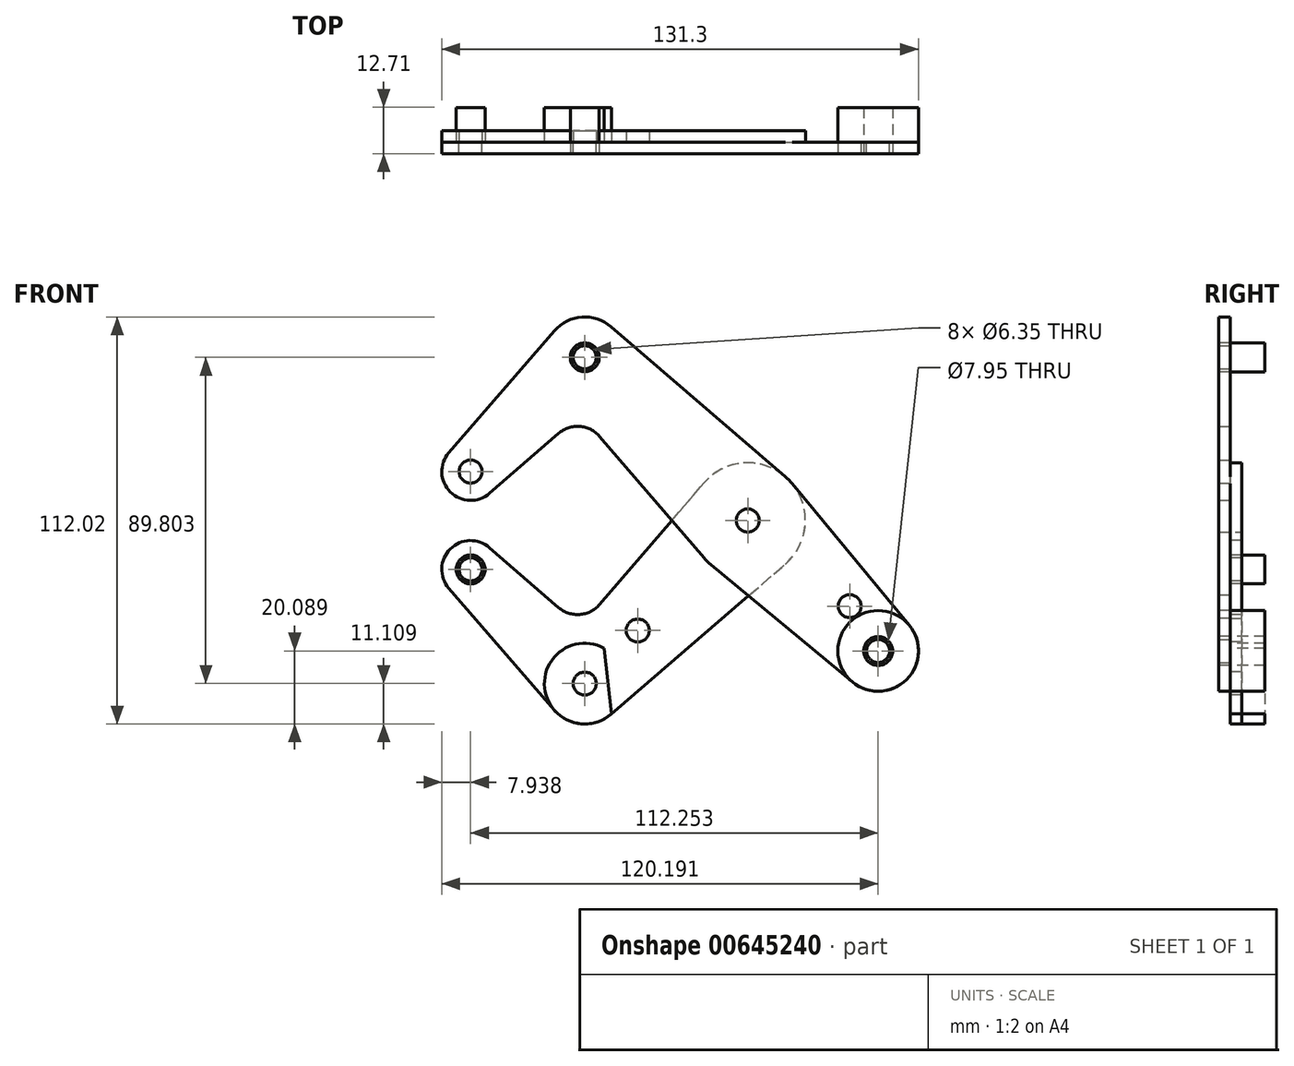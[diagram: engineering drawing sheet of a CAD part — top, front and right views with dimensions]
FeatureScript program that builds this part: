
annotation { "Feature Type Name" : "Feature", "Feature Type Description" : "" }
export const myFeature = defineFeature(function(context is Context, id is Id, definition is map)
    precondition{}
    {
        {
            var Q0;
            Q0=qCreatedBy(makeId("Front.planeOp"),FACE);
            var sketch = newSketch(context, id + "F0", { "sketchPlane" : qUnion([Q0])});
            skLineSegment(sketch, "E0", {"start": v(-76.33, 13.47) * mm, "end": v(-44.9, 44.9) * mm, "construction": true});
            skLineSegment(sketch, "E1", {"start": v(-44.9, 44.9) * mm, "end": v(35.92, -35.92) * mm, "construction": true});
            skCircle(sketch, "E2", {"center": v(-76.33, 13.47) * mm, "radius": 3.18 * mm});
            skCircle(sketch, "E3", {"center": v(-44.9, 44.9) * mm, "radius": 3.18 * mm});
            skCircle(sketch, "E4", {"center": v(35.92, -35.92) * mm, "radius": 3.18 * mm});
            skCircle(sketch, "E5", {"center": v(0, 0) * mm, "radius": 3.18 * mm});
            skCircle(sketch, "E6", {"center": v(35.92, -35.92) * mm, "radius": 11.11 * mm});
            skCircle(sketch, "E7", {"center": v(-44.9, 44.9) * mm, "radius": 11.11 * mm});
            skCircle(sketch, "E8", {"center": v(0, 0) * mm, "radius": 3.98 * mm});
            skCircle(sketch, "E9", {"center": v(-76.33, 13.47) * mm, "radius": 7.94 * mm});
            skCircle(sketch, "E10", {"center": v(0, 0) * mm, "radius": 15.88 * mm});
            skCircle(sketch, "E11", {"center": v(28.07, -23.58) * mm, "radius": 3.18 * mm});
            skLineSegment(sketch, "E12", {"start": v(0, 0) * mm, "end": v(31.58, 31.58) * mm, "construction": true});
            skLineSegment(sketch, "E13", {"start": v(0, 0) * mm, "end": v(-44.9, -44.9) * mm, "construction": true});
            skLineSegment(sketch, "E14", {"start": v(-76.33, -13.47) * mm, "end": v(-44.9, -44.9) * mm, "construction": true});
            skCircle(sketch, "E15", {"center": v(-44.9, -44.9) * mm, "radius": 3.18 * mm});
            skCircle(sketch, "E16", {"center": v(-76.33, -13.47) * mm, "radius": 3.18 * mm});
            skCircle(sketch, "E17", {"center": v(-30.3, -30.3) * mm, "radius": 3.18 * mm});
            skCircle(sketch, "E18", {"center": v(-76.33, -13.47) * mm, "radius": 7.94 * mm});
            skCircle(sketch, "E19", {"center": v(-44.9, -44.9) * mm, "radius": 11.11 * mm});
            skLineSegment(sketch, "E20", {"start": v(10.35, 12.04) * mm, "end": v(-37.66, 53.33) * mm});
            skLineSegment(sketch, "E21", {"start": v(-53.3, 52.18) * mm, "end": v(-82.33, 18.67) * mm});
            skLineSegment(sketch, "E22", {"start": v(12.23, 10.12) * mm, "end": v(44.48, -28.83) * mm});
            skLineSegment(sketch, "E23", {"start": v(28.83, -44.48) * mm, "end": v(-10.12, -12.23) * mm});
            skLineSegment(sketch, "E24", {"start": v(-53.33, -37.66) * mm, "end": v(-52.78, -37.02) * mm});
            skLineSegment(sketch, "E25", {"start": v(-71.13, 7.47) * mm, "end": v(-52.08, 23.98) * mm});
            skLineSegment(sketch, "E26", {"start": v(-53.33, 37.66) * mm, "end": v(-52.78, 37.02) * mm});
            skLineSegment(sketch, "E27", {"start": v(-37.66, -53.33) * mm, "end": v(10.35, -12.04) * mm});
            skLineSegment(sketch, "E28", {"start": v(-52.08, -23.98) * mm, "end": v(-71.13, -7.47) * mm});
            skLineSegment(sketch, "E29", {"start": v(-82.33, -18.67) * mm, "end": v(-53.3, -52.18) * mm});
            skLineSegment(sketch, "E30.trimOffspring", {"start": v(-40.85, 23.15) * mm, "end": v(-12.04, -10.35) * mm});
            skLineSegment(sketch, "E31.trimOffspring", {"start": v(-40.85, -23.15) * mm, "end": v(-12.04, 10.35) * mm});
            skLineSegment(sketch, "E32", {"start": v(-76.33, 13.47) * mm, "end": v(-76.33, -46.2) * mm, "construction": true});
            skPoint(sketch, "E33.visualSharp", {"position": v(-46.05, 29.2) * mm});
            skArc(sketch, "E33.filletArc", {"start": v(-40.85, 23.15) * mm, "mid": v(-46.3, 25.9) * mm, "end": v(-52.08, 23.98) * mm});
            skPoint(sketch, "E34.visualSharp", {"position": v(-46.05, -29.2) * mm});
            skArc(sketch, "E34.filletArc", {"start": v(-52.08, -23.98) * mm, "mid": v(-46.3, -25.9) * mm, "end": v(-40.85, -23.15) * mm});
            skLineSegment(sketch, "E35", {"start": v(35.92, -35.92) * mm, "end": v(-44.9, -44.9) * mm, "construction": true});
            skSolve(sketch);
        }
        {
            var Q0;
            {var subQ3=sQuery(id+"F0.wireOp",EDGE,"E20");Q0=makeQuery(id+"F0.imprint","IMPRINT",FACE,{"disambiguationData":[TD([[makeQuery(id+"F0.imprint","IMPRINT",EDGE,{"derivedFrom":subQ3}),1.0]])]});}
            var Q1;
            Q1=makeQuery(id+"F0.imprint","IMPRINT",FACE,{"disambiguationData":[TD([[makeQuery(id+"F0.imprint","IMPRINT",EDGE,{"derivedFrom":sQuery(id+"F0.wireOp",EDGE,"E11")}),-1.0]])]});
            var Q2;
            Q2=makeQuery(id+"F0.imprint","IMPRINT",FACE,{"disambiguationData":[TD([[makeQuery(id+"F0.imprint","IMPRINT",EDGE,{"derivedFrom":sQuery(id+"F0.wireOp",EDGE,"E8")}),-1.0]])]});
            var Q3;
            {var subQ0=sQuery(id+"F0.wireOp",EDGE,"E23");var subQ1=sQuery(id+"F0.wireOp",EDGE,"E10");var subQ2=makeQuery(id+"F0.imprint","INTERSECT",VERTEX,{"derivedFrom":[subQ1,subQ0]});Q3=makeQuery(id+"F0.imprint","IMPRINT",FACE,{"disambiguationData":[TD([[makeQuery(id+"F0.imprint","IMPRINT",EDGE,{"disambiguationData":[TD([[subQ2,-1.0]])],"derivedFrom":subQ1}),-1.0]])]});}
            var Q4;
            {var subQ0=sQuery(id+"F0.wireOp",EDGE,"E30.trimOffspring");var subQ1=sQuery(id+"F0.wireOp",EDGE,"E10");var subQ2=makeQuery(id+"F0.imprint","INTERSECT",VERTEX,{"derivedFrom":[subQ1,subQ0]});Q4=makeQuery(id+"F0.imprint","IMPRINT",FACE,{"disambiguationData":[TD([[makeQuery(id+"F0.imprint","IMPRINT",EDGE,{"disambiguationData":[TD([[subQ2,1.0]])],"derivedFrom":subQ1}),-1.0]])]});}
            var Q5;
            Q5=makeQuery(id+"F0.imprint","IMPRINT",FACE,{"disambiguationData":[TD([[makeQuery(id+"F0.imprint","IMPRINT",EDGE,{"derivedFrom":sQuery(id+"F0.wireOp",EDGE,"E3")}),-1.0]])]});
            var Q6;
            Q6=makeQuery(id+"F0.imprint","IMPRINT",FACE,{"disambiguationData":[TD([[makeQuery(id+"F0.imprint","IMPRINT",EDGE,{"derivedFrom":sQuery(id+"F0.wireOp",EDGE,"E2")}),-1.0]])]});
            var Q7;
            Q7=makeQuery(id+"F0.imprint","IMPRINT",FACE,{"disambiguationData":[TD([[makeQuery(id+"F0.imprint","IMPRINT",EDGE,{"derivedFrom":sQuery(id+"F0.wireOp",EDGE,"E4")}),-1.0]])]});
            extrude(context, id + "F1", {"entities" : qUnion([Q0, Q1, Q2, Q3, Q4, Q5, Q6, Q7]), "depth" : 3.17 * mm, "offsetDistance" : 25.4 * mm});
        }
        {
            var Q0;
            Q0=makeQuery(id+"F0.imprint","IMPRINT",FACE,{"disambiguationData":[TD([[makeQuery(id+"F0.imprint","IMPRINT",EDGE,{"derivedFrom":sQuery(id+"F0.wireOp",EDGE,"E17")}),-1.0]])]});
            var Q1;
            {var subQ0=sQuery(id+"F0.wireOp",EDGE,"E30.trimOffspring");var subQ1=sQuery(id+"F0.wireOp",EDGE,"E10");var subQ2=makeQuery(id+"F0.imprint","INTERSECT",VERTEX,{"derivedFrom":[subQ1,subQ0]});Q1=makeQuery(id+"F0.imprint","IMPRINT",FACE,{"disambiguationData":[TD([[makeQuery(id+"F0.imprint","IMPRINT",EDGE,{"disambiguationData":[TD([[subQ2,1.0]])],"derivedFrom":subQ1}),-1.0]])]});}
            var Q2;
            Q2=makeQuery(id+"F0.imprint","IMPRINT",FACE,{"disambiguationData":[TD([[makeQuery(id+"F0.imprint","IMPRINT",EDGE,{"derivedFrom":sQuery(id+"F0.wireOp",EDGE,"E8")}),-1.0]])]});
            var Q3;
            Q3=makeQuery(id+"F0.imprint","IMPRINT",FACE,{"disambiguationData":[TD([[makeQuery(id+"F0.imprint","IMPRINT",EDGE,{"derivedFrom":sQuery(id+"F0.wireOp",EDGE,"E15")}),-1.0]])]});
            var Q4;
            Q4=makeQuery(id+"F0.imprint","IMPRINT",FACE,{"disambiguationData":[TD([[makeQuery(id+"F0.imprint","IMPRINT",EDGE,{"derivedFrom":sQuery(id+"F0.wireOp",EDGE,"E16")}),-1.0]])]});
            var Q5;
            {var subQ0=sQuery(id+"F0.wireOp",EDGE,"E23");var subQ1=sQuery(id+"F0.wireOp",EDGE,"E10");var subQ2=makeQuery(id+"F0.imprint","INTERSECT",VERTEX,{"derivedFrom":[subQ1,subQ0]});Q5=makeQuery(id+"F0.imprint","IMPRINT",FACE,{"disambiguationData":[TD([[makeQuery(id+"F0.imprint","IMPRINT",EDGE,{"disambiguationData":[TD([[subQ2,-1.0]])],"derivedFrom":subQ1}),-1.0]])]});}
            extrude(context, id + "F2", {"entities" : qUnion([Q0, Q1, Q2, Q3, Q4, Q5]), "oppositeDirection" : true, "depth" : 3.17 * mm, "offsetDistance" : 25.4 * mm});
        }
        {
            var Q0;
            Q0=makeQuery(id+"F0.imprint","IMPRINT",FACE,{"disambiguationData":[TD([[makeQuery(id+"F0.imprint","IMPRINT",EDGE,{"derivedFrom":sQuery(id+"F0.wireOp",EDGE,"E5")}),-1.0]])]});
            extrude(context, id + "F3", {"entities" : qUnion([Q0]), "operationType" : NewBodyOperationType.ADD, "depth" : 3.17 * mm, "offsetDistance" : 25.4 * mm, "hasSecondDirection" : true, "secondDirectionOppositeDirection" : true, "secondDirectionDepth" : 3.17 * mm});
        }
        {
            var Q0;
            Q0=makeQuery(id+"F1.opExtrude","CAP_FACE",FACE,{"disambiguationData":[OSD([sQuery(id+"F0.wireOp",EDGE,"E2"),sQuery(id+"F0.wireOp",EDGE,"E3"),sQuery(id+"F0.wireOp",EDGE,"E4"),sQuery(id+"F0.wireOp",EDGE,"E6"),sQuery(id+"F0.wireOp",EDGE,"E7"),sQuery(id+"F0.wireOp",EDGE,"E8"),sQuery(id+"F0.wireOp",EDGE,"E9"),sQuery(id+"F0.wireOp",EDGE,"E10"),sQuery(id+"F0.wireOp",EDGE,"E11"),sQuery(id+"F0.wireOp",EDGE,"E20"),sQuery(id+"F0.wireOp",EDGE,"E21"),sQuery(id+"F0.wireOp",EDGE,"E22"),sQuery(id+"F0.wireOp",EDGE,"E23"),sQuery(id+"F0.wireOp",EDGE,"E25"),sQuery(id+"F0.wireOp",EDGE,"E30.trimOffspring"),sQuery(id+"F0.wireOp",EDGE,"E33.filletArc")])],"isStart":false});
            var sketch = newSketch(context, id + "F4", { "sketchPlane" : qUnion([Q0])});
            skCircle(sketch, "E36", {"center": v(-44.9, 44.9) * mm, "radius": 3.98 * mm});
            skCircle(sketch, "E37", {"center": v(35.92, -35.92) * mm, "radius": 11.11 * mm});
            skLineSegment(sketch, "E38", {"start": v(-39.6, -35.14) * mm, "end": v(-37.58, -53.26) * mm});
            skArc(sketch, "E39", {"start": v(-39.6, -35.14) * mm, "mid": v(-55.95, -46.13) * mm, "end": v(-37.58, -53.26) * mm});
            skCircle(sketch, "E40", {"center": v(-76.33, -13.47) * mm, "radius": 3.98 * mm});
            skCircle(sketch, "E41", {"center": v(35.92, -35.92) * mm, "radius": 3.98 * mm});
            skSolve(sketch);
        }
        {
            var Q0;
            Q0=qCreatedBy(makeId("Front.planeOp"),FACE);
            cPlane(context, id + "F5", {"entities" : qUnion([Q0]), "cplaneType" : CPlaneType.OFFSET, "offset" : 9.52 * mm, "oppositeDirection" : true, "width" : 152.4 * mm, "height" : 152.4 * mm});
        }
        {
            var Q0;
            Q0=makeQuery(id+"F4.imprint","IMPRINT",FACE,{"disambiguationData":[TD([[makeQuery(id+"F4.imprint","IMPRINT",EDGE,{"derivedFrom":makeQuery(id+"F1.opExtrude","CAP_EDGE",EDGE,{"disambiguationData":[OSD([sQuery(id+"F0.wireOp",EDGE,"E3")])],"isStart":false})}),1.0]])]});
            var Q1;
            Q1=makeQuery(id+"F4.imprint","IMPRINT",FACE,{"disambiguationData":[TD([[makeQuery(id+"F4.imprint","IMPRINT",EDGE,{"derivedFrom":sQuery(id+"F4.wireOp",EDGE,"E36")}),1.0]])]});
            var Q2;
            Q2=makeQuery(id+"F4.imprint","IMPRINT",FACE,{"disambiguationData":[TD([[makeQuery(id+"F4.imprint","IMPRINT",EDGE,{"derivedFrom":sQuery(id+"F4.wireOp",EDGE,"E41")}),-1.0]])]});
            var Q3;
            Q3=qCreatedBy(id+"F5.planeOp",FACE);
            extrude(context, id + "F6", {"entities" : qUnion([Q0, Q1, Q2]), "endBound" : BoundingType.UP_TO_SURFACE, "oppositeDirection" : true, "depth" : 25.4 * mm, "endBoundEntityFace" : qUnion([Q3]), "offsetDistance" : 25.4 * mm});
        }
        {
            var Q0;
            Q0=makeQuery(id+"F4.imprint","IMPRINT",FACE,{"disambiguationData":[TD([[makeQuery(id+"F4.imprint","IMPRINT",EDGE,{"derivedFrom":sQuery(id+"F4.wireOp",EDGE,"E38")}),-1.0]])]});
            var Q1;
            Q1=makeQuery(id+"F4.imprint","IMPRINT",FACE,{"disambiguationData":[TD([[makeQuery(id+"F4.imprint","IMPRINT",EDGE,{"derivedFrom":sQuery(id+"F4.wireOp",EDGE,"E40")}),1.0]])]});
            var Q2;
            Q2=qCreatedBy(id+"F5.planeOp",FACE);
            var Q3;
            Q3=qCreatedBy(makeId("Front.planeOp"),FACE);
            extrude(context, id + "F7", {"entities" : qUnion([Q0, Q1]), "endBound" : BoundingType.UP_TO_SURFACE, "oppositeDirection" : true, "depth" : 25.4 * mm, "endBoundEntityFace" : qUnion([Q2]), "offsetDistance" : 25.4 * mm, "hasSecondDirection" : true, "secondDirectionBound" : SecondDirectionBoundingType.UP_TO_SURFACE, "secondDirectionOppositeDirection" : true, "secondDirectionDepth" : 4.83 * mm, "secondDirectionBoundEntityFace" : qUnion([Q3])});
        }
    });
